# Revit family: nbl_TritonSystems_AquaChannel-ChannelRoddingEye
name_source: partatom
category: Plumbing Fixtures
revit_build: Autodesk Revit Architecture 2012 (Build: 20110309_2315(x64)
units: mm (PartAtom-declared; Revit-internal decimal feet)

## types (1)
- nbl_TritonSystems_AquaChannel-ChannelRoddingEye
    BIMObjectName = nbl_TritonSystems_AquaChannel-RoddingEye
    Colour = Grey and Black
    Description = PVC drainage conduit
    DocumentReference = www.tritonsystems.co.uk
    Documentation = www.tritonsystems.co.uk/pdf/Triton_Pumps_Brochure.pdf
    DrainHoles = 19 mm
    Help = www.nationalBIMlibrary.com
    IssueDate = 2012-11-26
    Manufacturer = Triton Systems
    ManufacturerURL = www.tritonsystems.co.uk
    Material = PVC
    ModelReference = Triton Aqua Channel Rodding Eye
    NBSDescription = Floor channels
    NBSReference = 90-05-20/302
    NominalHeight = 0 mm  [stored 0 ft]
    NominalLength = 0 mm  [stored 0 ft]
    NominalWidth = 80 mm  [stored 0.262467 ft]
    Shape = Rectangle
    Size = 80 mm x Varied mm
    StandardHeight = Varies
    StandardLength = 2000 mm
    StandardWidth = 80 mm
    THeight = 100 mm  [stored 0.328084 ft]
    Version = 1.0

note: [stored X ft] marks values corroborated as IEEE doubles in the binary element streams (Revit-internal decimal feet)

## geometry (parser evidence)
native form markers: Sweep x3
no freeform markers — native parametric forms only
